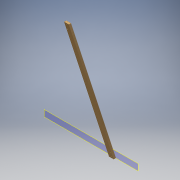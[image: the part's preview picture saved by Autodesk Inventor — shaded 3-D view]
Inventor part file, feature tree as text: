
AUTODESK INVENTOR PART (.ipt)
format: ipt  version: 2017 (Build 210142000, 142)  size: 112,640 bytes
history: native  units: in
note: dims shown in document units (in); Inventor stores cm internally (conversion verified against a paired STEP export)
features: reference x13, other x8, plane x1, extrude x1, sketch x1
ambient origin geometry x8: Origin, YZ Plane, XZ Plane, XY Plane, X Axis, Y Axis, Z Axis, Center Point
bodies: Solid1 (feature_tree)
feature tree (24):
  plane  "Work Plane1"
  extrude  "Extrusion1"  Depth=0.7585in
  sketch  "Sketch1"  dims[d0=1.45in d1=1.5662in d2=0.7585in d3=0.0in]
  reference  "Reference1"
  reference  "Reference2"
  reference  "Reference3"
  reference  "Reference4"
  reference  "Reference5"
  reference  "Reference6"
  reference  "Reference7"
  reference  "Reference8"
  reference  "Reference9"
  reference  "Reference10"
  reference  "Reference11"
  reference  "Reference12"
  reference  "Reference13"
  other  "<userpath>\Documents\Inventor\2017 Robot\Robot Chassis - The actual one.iam"
  other  "Robot Chassis - The actual one.iam"
  other  "End Sheet - 28.5:1"
  other  "End Sheet - 28.5:2"
  other  "Robot Chassis Half:2"
  other  "am-0255+2.5inch+CIM+Motor:1"
  other  "Robot Chassis Half:1"
  other  "am-2952a_AM14U3_Inside_Plate:1"
